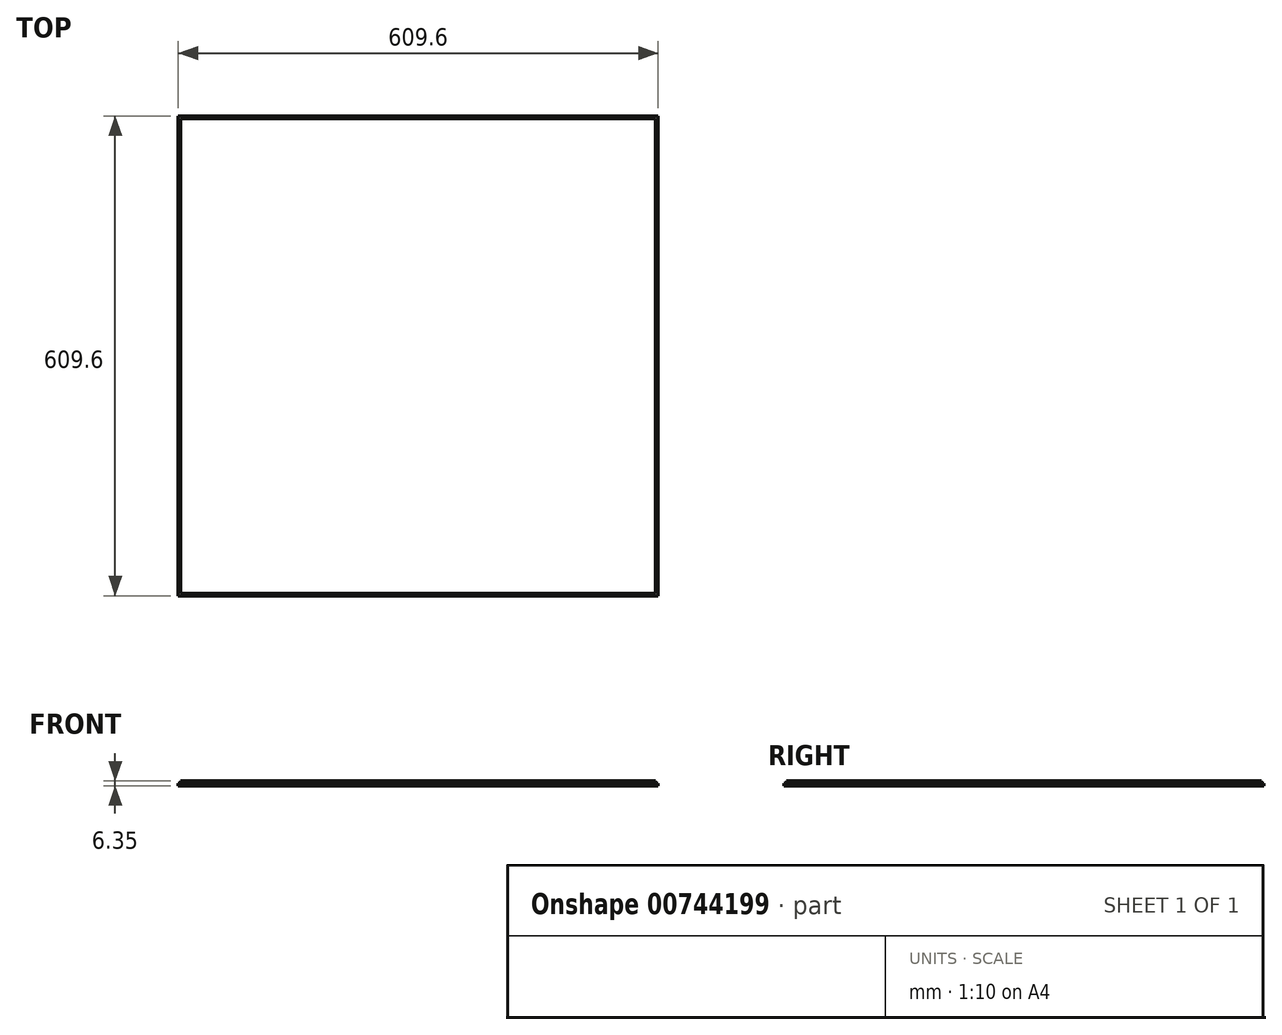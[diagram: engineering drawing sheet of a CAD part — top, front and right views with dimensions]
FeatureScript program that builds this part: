
annotation { "Feature Type Name" : "Feature", "Feature Type Description" : "" }
export const myFeature = defineFeature(function(context is Context, id is Id, definition is map)
    precondition{}
    {
        {
            var Q0;
            Q0=qCreatedBy(makeId("Top.planeOp"),FACE);
            var sketch = newSketch(context, id + "F0", { "sketchPlane" : qUnion([Q0])});
            skLineSegment(sketch, "E0", {"start": v(0, 304.8) * mm, "end": v(0, -304.8) * mm, "construction": true});
            skLineSegment(sketch, "E1", {"start": v(-304.8, 0) * mm, "end": v(304.8, 0) * mm, "construction": true});
            skLineSegment(sketch, "E2.bottom", {"start": v(-304.8, 304.8) * mm, "end": v(304.8, 304.8) * mm});
            skLineSegment(sketch, "E2.top", {"start": v(-304.8, -304.8) * mm, "end": v(304.8, -304.8) * mm});
            skLineSegment(sketch, "E2.left", {"start": v(-304.8, 304.8) * mm, "end": v(-304.8, -304.8) * mm});
            skLineSegment(sketch, "E2.right", {"start": v(304.8, 304.8) * mm, "end": v(304.8, -304.8) * mm});
            skSolve(sketch);
        }
        {
            var Q0;
            Q0 = qSketchRegion(id + "F0", true);
            extrude(context, id + "F1", {"entities" : qUnion([Q0]), "depth" : 6.35 * mm, "offsetDistance" : 25.4 * mm});
        }
        {
            var Q0;
            Q0=makeQuery(id+"F1.opExtrude","CAP_FACE",FACE,{"disambiguationData":[OSD([sQuery(id+"F0.wireOp",EDGE,"E2.bottom"),sQuery(id+"F0.wireOp",EDGE,"E2.top"),sQuery(id+"F0.wireOp",EDGE,"E2.left"),sQuery(id+"F0.wireOp",EDGE,"E2.right")])],"isStart":false});
            var sketch = newSketch(context, id + "F2", { "sketchPlane" : qUnion([Q0])});
            skLineSegment(sketch, "E3.0", {"start": v(-301.62, 301.63) * mm, "end": v(-301.63, -301.63) * mm});
            skLineSegment(sketch, "E3.1", {"start": v(301.63, 301.63) * mm, "end": v(-301.62, 301.63) * mm});
            skLineSegment(sketch, "E3.2", {"start": v(301.63, -301.63) * mm, "end": v(301.63, 301.63) * mm});
            skLineSegment(sketch, "E3.3", {"start": v(-301.63, -301.63) * mm, "end": v(301.63, -301.63) * mm});
            skSolve(sketch);
        }
        {
            var Q0;
            Q0=makeQuery(id+"F2.imprint","IMPRINT",FACE,{"disambiguationData":[TD([[makeQuery(id+"F2.imprint","IMPRINT",EDGE,{"derivedFrom":sQuery(id+"F2.wireOp",EDGE,"E3.0")}),-1.0]])]});
            extrude(context, id + "F3", {"entities" : qUnion([Q0]), "operationType" : NewBodyOperationType.REMOVE, "oppositeDirection" : true, "depth" : 3.17 * mm, "offsetDistance" : 25.4 * mm});
        }
    });
